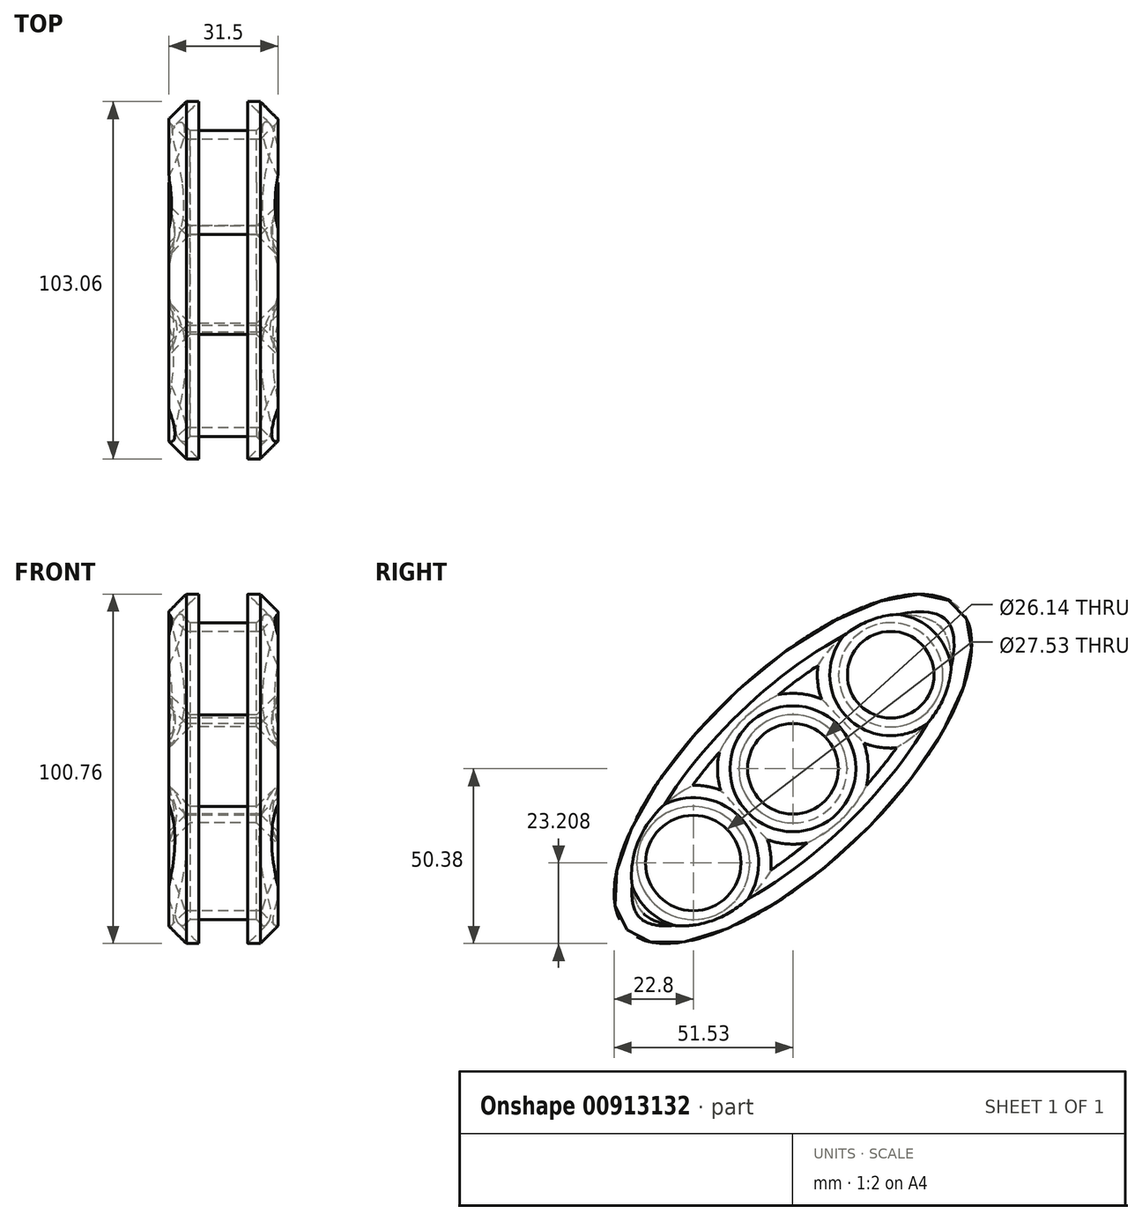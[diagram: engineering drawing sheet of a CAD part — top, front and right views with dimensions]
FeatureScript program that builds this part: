
annotation { "Feature Type Name" : "Feature", "Feature Type Description" : "" }
export const myFeature = defineFeature(function(context is Context, id is Id, definition is map)
    precondition{}
    {
        {
            var Q0;
            Q0=qCreatedBy(makeId("Right.planeOp"),FACE);
            var sketch = newSketch(context, id + "F0", { "sketchPlane" : qUnion([Q0])});
            skEllipse(sketch, "E0", {"center": v(0, 0) * mm, "majorRadius": 66.68 * mm, "minorRadius": 27.33 * mm, "majorAxis": v(-0.72, -0.7)});
            skCircle(sketch, "E1", {"center": v(0, 0) * mm, "radius": 13.07 * mm});
            skCircle(sketch, "E2", {"center": v(28.2, 27.12) * mm, "radius": 12.5 * mm});
            skCircle(sketch, "E3", {"center": v(-28.73, -27.17) * mm, "radius": 13.76 * mm});
            skSolve(sketch);
        }
        {
            var Q0;
            Q0 = qSketchRegion(id + "F0", true);
            extrude(context, id + "F1", {"entities" : qUnion([Q0]), "depth" : 31.5 * mm, "offsetDistance" : 25.4 * mm});
        }
        {
            var Q0;
            Q0=makeQuery(id+"F1.opExtrude","CAP_EDGE",EDGE,{"disambiguationData":[OSD([sQuery(id+"F0.wireOp",EDGE,"E0")])],"isStart":false});
            var Q1;
            Q1=makeQuery(id+"F1.opExtrude","CAP_EDGE",EDGE,{"disambiguationData":[OSD([sQuery(id+"F0.wireOp",EDGE,"E0")])],"isStart":true});
            var Q2;
            Q2=makeQuery(id+"F1.opExtrude","CAP_EDGE",EDGE,{"disambiguationData":[OSD([sQuery(id+"F0.wireOp",EDGE,"E1")])],"isStart":false});
            var Q3;
            Q3=makeQuery(id+"F1.opExtrude","CAP_EDGE",EDGE,{"disambiguationData":[OSD([sQuery(id+"F0.wireOp",EDGE,"E3")])],"isStart":false});
            var Q4;
            Q4=makeQuery(id+"F1.opExtrude","CAP_EDGE",EDGE,{"disambiguationData":[OSD([sQuery(id+"F0.wireOp",EDGE,"E2")])],"isStart":false});
            var Q5;
            Q5=makeQuery(id+"F1.opExtrude","CAP_EDGE",EDGE,{"disambiguationData":[OSD([sQuery(id+"F0.wireOp",EDGE,"E2")])],"isStart":true});
            var Q6;
            Q6=makeQuery(id+"F1.opExtrude","CAP_EDGE",EDGE,{"disambiguationData":[OSD([sQuery(id+"F0.wireOp",EDGE,"E1")])],"isStart":true});
            var Q7;
            Q7=makeQuery(id+"F1.opExtrude","CAP_EDGE",EDGE,{"disambiguationData":[OSD([sQuery(id+"F0.wireOp",EDGE,"E3")])],"isStart":true});
            chamfer(context, id + "F2", {"entities" : qUnion([Q0, Q1, Q2, Q3, Q4, Q5, Q6, Q7]), "width" : 5.08 * mm, "tangentPropagation" : true});
        }
        {
            var Q0;
            Q0=makeQuery(id+"F2.opChamfer","SPLIT",FACE,{"disambiguationData":[OD(2.0)],"derivedFrom":makeQuery(id+"F1.opExtrude","CAP_FACE",FACE,{"disambiguationData":[OSD([sQuery(id+"F0.wireOp",EDGE,"E0"),sQuery(id+"F0.wireOp",EDGE,"E1"),sQuery(id+"F0.wireOp",EDGE,"E2"),sQuery(id+"F0.wireOp",EDGE,"E3")])],"isStart":true})});
            var Q1;
            Q1=makeQuery(id+"F2.opChamfer","SPLIT",FACE,{"disambiguationData":[OD(2.0)],"derivedFrom":makeQuery(id+"F1.opExtrude","CAP_FACE",FACE,{"disambiguationData":[OSD([sQuery(id+"F0.wireOp",EDGE,"E0"),sQuery(id+"F0.wireOp",EDGE,"E1"),sQuery(id+"F0.wireOp",EDGE,"E2"),sQuery(id+"F0.wireOp",EDGE,"E3")])],"isStart":false})});
            var Q2;
            Q2=makeQuery(id+"F2.opChamfer","SPLIT",FACE,{"disambiguationData":[OD(0.0)],"derivedFrom":makeQuery(id+"F1.opExtrude","CAP_FACE",FACE,{"disambiguationData":[OSD([sQuery(id+"F0.wireOp",EDGE,"E0"),sQuery(id+"F0.wireOp",EDGE,"E1"),sQuery(id+"F0.wireOp",EDGE,"E2"),sQuery(id+"F0.wireOp",EDGE,"E3")])],"isStart":true})});
            var Q3;
            Q3=makeQuery(id+"F2.opChamfer","SPLIT",FACE,{"disambiguationData":[OD(1.0)],"derivedFrom":makeQuery(id+"F1.opExtrude","CAP_FACE",FACE,{"disambiguationData":[OSD([sQuery(id+"F0.wireOp",EDGE,"E0"),sQuery(id+"F0.wireOp",EDGE,"E1"),sQuery(id+"F0.wireOp",EDGE,"E2"),sQuery(id+"F0.wireOp",EDGE,"E3")])],"isStart":true})});
            var Q4;
            Q4=makeQuery(id+"F2.opChamfer","SPLIT",FACE,{"disambiguationData":[OD(1.0)],"derivedFrom":makeQuery(id+"F1.opExtrude","CAP_FACE",FACE,{"disambiguationData":[OSD([sQuery(id+"F0.wireOp",EDGE,"E0"),sQuery(id+"F0.wireOp",EDGE,"E1"),sQuery(id+"F0.wireOp",EDGE,"E2"),sQuery(id+"F0.wireOp",EDGE,"E3")])],"isStart":false})});
            var Q5;
            Q5=makeQuery(id+"F2.opChamfer","SPLIT",FACE,{"disambiguationData":[OD(0.0)],"derivedFrom":makeQuery(id+"F1.opExtrude","CAP_FACE",FACE,{"disambiguationData":[OSD([sQuery(id+"F0.wireOp",EDGE,"E0"),sQuery(id+"F0.wireOp",EDGE,"E1"),sQuery(id+"F0.wireOp",EDGE,"E2"),sQuery(id+"F0.wireOp",EDGE,"E3")])],"isStart":false})});
            var Q6;
            Q6=makeQuery(id+"F1.opExtrude","SWEPT_FACE",FACE,{"disambiguationData":[OSD([sQuery(id+"F0.wireOp",EDGE,"E0")])]});
            shell(context, id + "F3", {"entities" : qUnion([Q0, Q1, Q2, Q3, Q4, Q5, Q6]), "thickness" : 2.54 * mm});
        }
    });
